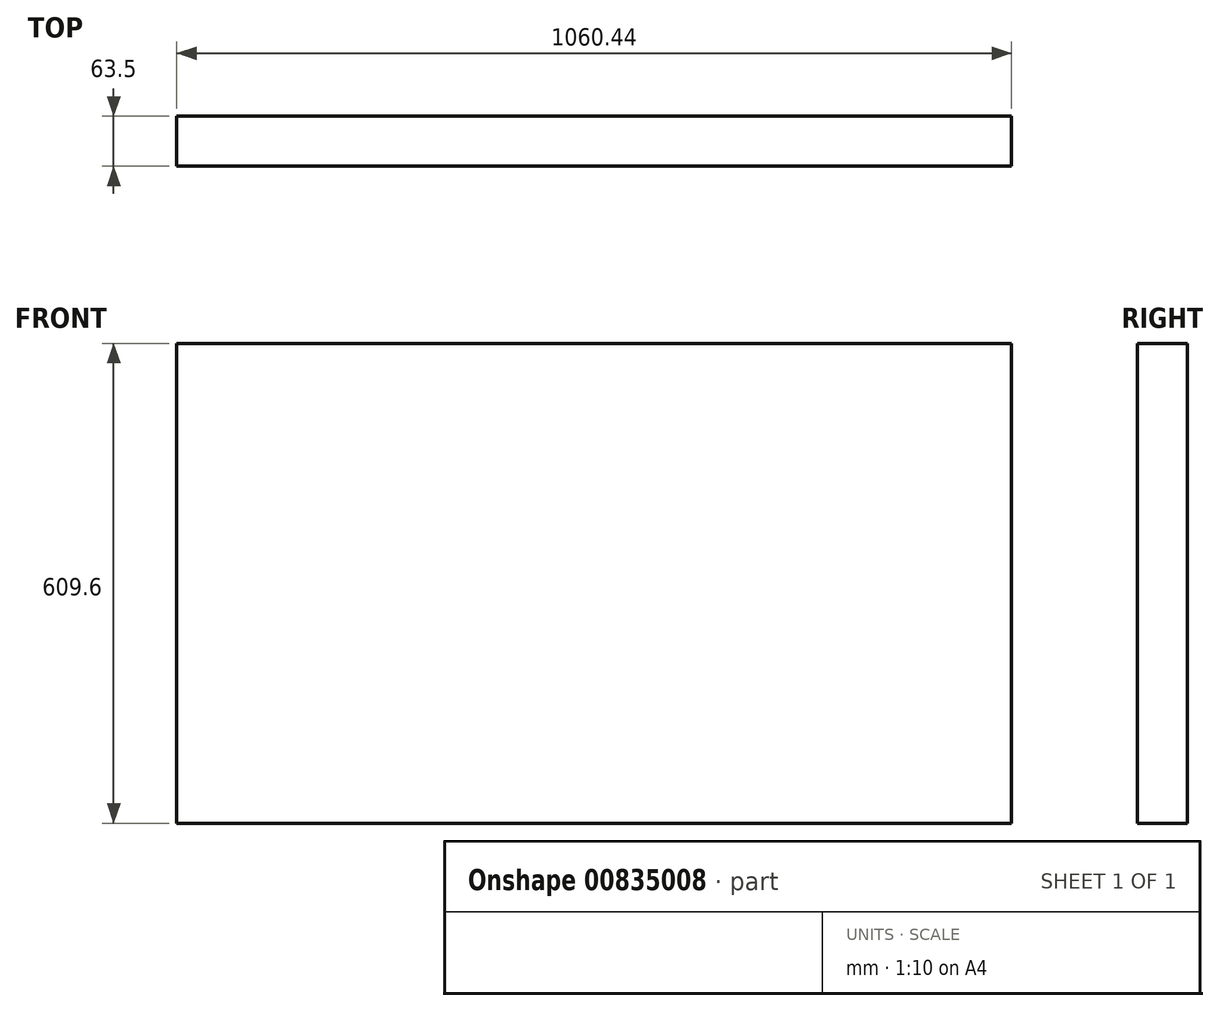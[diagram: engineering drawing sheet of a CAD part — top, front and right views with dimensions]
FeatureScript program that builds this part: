
annotation { "Feature Type Name" : "Feature", "Feature Type Description" : "" }
export const myFeature = defineFeature(function(context is Context, id is Id, definition is map)
    precondition{}
    {
        {
            var Q0;
            Q0=qCreatedBy(makeId("Front.planeOp"),FACE);
            var sketch = newSketch(context, id + "F0", { "sketchPlane" : qUnion([Q0])});
            skLineSegment(sketch, "E0.bottom", {"start": v(-530.23, 304.8) * mm, "end": v(530.23, 304.8) * mm});
            skLineSegment(sketch, "E0.top", {"start": v(-530.23, -304.8) * mm, "end": v(530.23, -304.8) * mm});
            skLineSegment(sketch, "E0.left", {"start": v(-530.23, 304.8) * mm, "end": v(-530.23, -304.8) * mm});
            skLineSegment(sketch, "E0.right", {"start": v(530.23, 304.8) * mm, "end": v(530.23, -304.8) * mm});
            skSolve(sketch);
        }
        {
            var Q0;
            Q0=makeQuery(id+"F0.imprint","IMPRINT",FACE,{"disambiguationData":[TD([[makeQuery(id+"F0.imprint","IMPRINT",EDGE,{"derivedFrom":sQuery(id+"F0.wireOp",EDGE,"E0.bottom")}),-1.0]])]});
            extrude(context, id + "F1", {"entities" : qUnion([Q0]), "depth" : 63.5 * mm, "offsetDistance" : 25.4 * mm});
        }
    });
